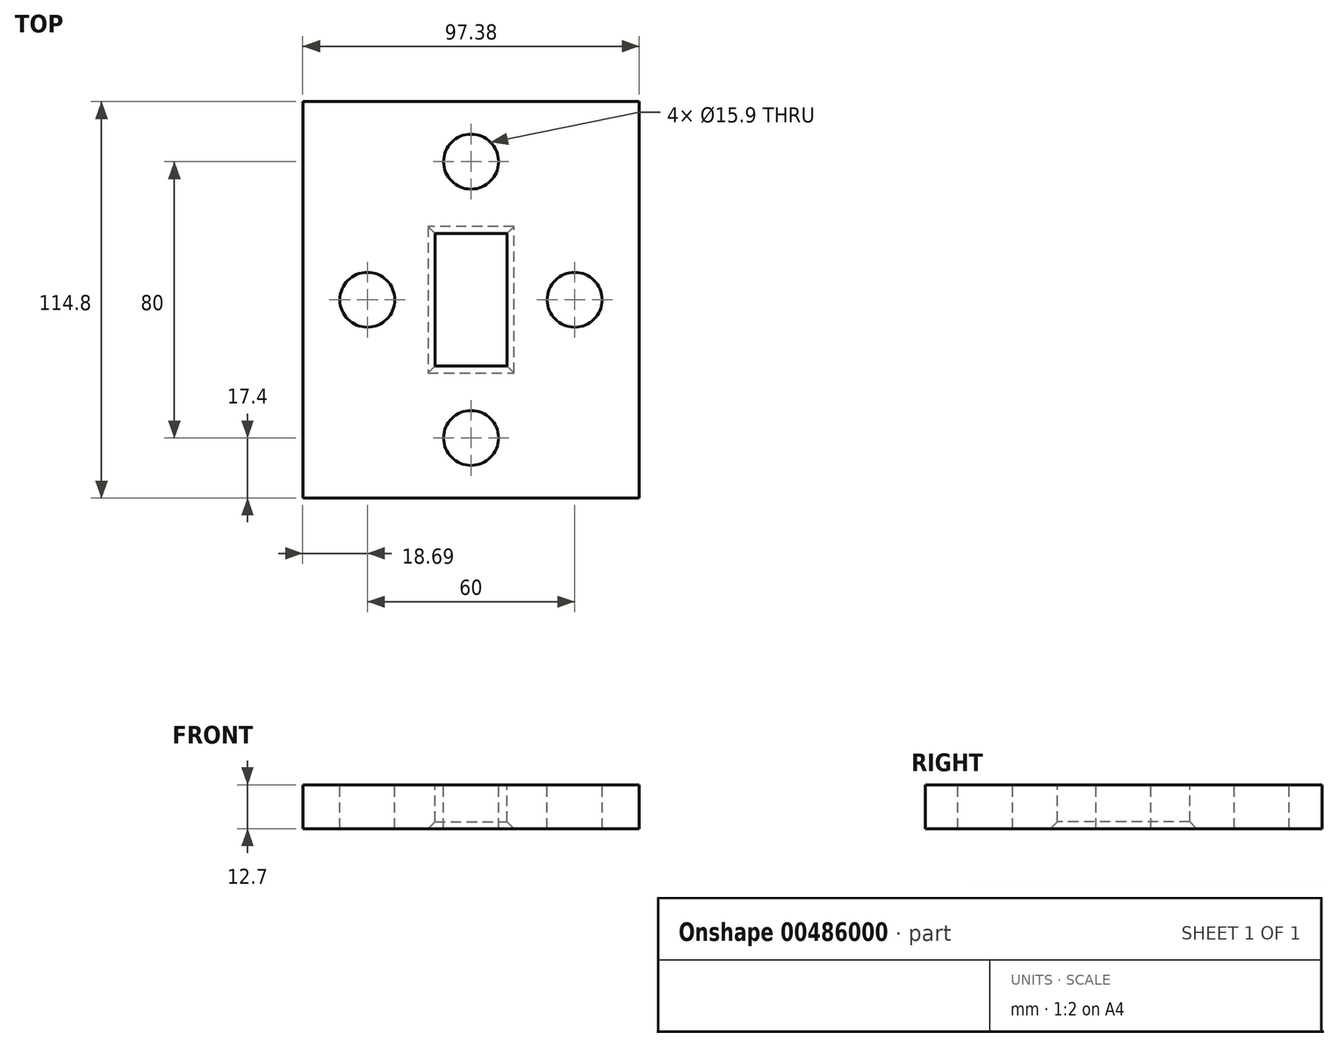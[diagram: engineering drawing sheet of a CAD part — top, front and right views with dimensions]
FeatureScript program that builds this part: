
annotation { "Feature Type Name" : "Feature", "Feature Type Description" : "" }
export const myFeature = defineFeature(function(context is Context, id is Id, definition is map)
    precondition{}
    {
        {
            var Q0;
            Q0=qCreatedBy(makeId("Top.planeOp"),FACE);
            var sketch = newSketch(context, id + "F0", { "sketchPlane" : qUnion([Q0])});
            skLineSegment(sketch, "E0.bottom", {"start": v(48.69, -57.4) * mm, "end": v(-48.69, -57.4) * mm});
            skLineSegment(sketch, "E0.top", {"start": v(48.69, 57.4) * mm, "end": v(-48.69, 57.4) * mm});
            skLineSegment(sketch, "E0.left", {"start": v(48.69, -57.4) * mm, "end": v(48.69, 57.4) * mm});
            skLineSegment(sketch, "E0.right", {"start": v(-48.69, -57.4) * mm, "end": v(-48.69, 57.4) * mm});
            skPoint(sketch, "E0.middle", {"position": v(0, 0) * mm});
            skSolve(sketch);
        }
        {
            var Q0;
            Q0 = qSketchRegion(id + "F0", true);
            extrude(context, id + "F1", {"entities" : qUnion([Q0]), "oppositeDirection" : true, "depth" : 12.7 * mm});
        }
        {
            var Q0;
            Q0=makeQuery(id+"F1.opExtrude","CAP_FACE",FACE,{"disambiguationData":[OSD([sQuery(id+"F0.wireOp",EDGE,"E0.bottom"),sQuery(id+"F0.wireOp",EDGE,"E0.top"),sQuery(id+"F0.wireOp",EDGE,"E0.left"),sQuery(id+"F0.wireOp",EDGE,"E0.right")])],"isStart":true});
            var sketch = newSketch(context, id + "F2", { "sketchPlane" : qUnion([Q0])});
            skLineSegment(sketch, "E1.bottom", {"start": v(10.47, 19.18) * mm, "end": v(-10.46, 19.18) * mm});
            skLineSegment(sketch, "E1.top", {"start": v(10.46, -19.18) * mm, "end": v(-10.47, -19.18) * mm});
            skLineSegment(sketch, "E1.left", {"start": v(10.47, 19.18) * mm, "end": v(10.46, -19.18) * mm});
            skLineSegment(sketch, "E1.right", {"start": v(-10.46, 19.18) * mm, "end": v(-10.47, -19.18) * mm});
            skPoint(sketch, "E1.middle", {"position": v(0, 0) * mm});
            skSolve(sketch);
        }
        {
            var Q0;
            Q0 = qSketchRegion(id + "F2", true);
            extrude(context, id + "F3", {"entities" : qUnion([Q0]), "operationType" : NewBodyOperationType.REMOVE, "endBound" : BoundingType.THROUGH_ALL, "oppositeDirection" : true, "depth" : 25 * mm});
        }
        {
            var Q0;
            Q0=makeQuery(id+"F3.boolean.opBoolean","INTERSECT",EDGE,{"derivedFrom":[makeQuery(id+"F1.opExtrude","CAP_FACE",FACE,{"disambiguationData":[OSD([sQuery(id+"F0.wireOp",EDGE,"E0.bottom"),sQuery(id+"F0.wireOp",EDGE,"E0.top"),sQuery(id+"F0.wireOp",EDGE,"E0.left"),sQuery(id+"F0.wireOp",EDGE,"E0.right")])],"isStart":false}),makeQuery(id+"F3.opExtrude","SWEPT_FACE",FACE,{"disambiguationData":[OSD([sQuery(id+"F2.wireOp",EDGE,"E1.bottom")])]})]});
            var Q1;
            Q1=makeQuery(id+"F3.boolean.opBoolean","INTERSECT",EDGE,{"derivedFrom":[makeQuery(id+"F1.opExtrude","CAP_FACE",FACE,{"disambiguationData":[OSD([sQuery(id+"F0.wireOp",EDGE,"E0.bottom"),sQuery(id+"F0.wireOp",EDGE,"E0.top"),sQuery(id+"F0.wireOp",EDGE,"E0.left"),sQuery(id+"F0.wireOp",EDGE,"E0.right")])],"isStart":false}),makeQuery(id+"F3.opExtrude","SWEPT_FACE",FACE,{"disambiguationData":[OSD([sQuery(id+"F2.wireOp",EDGE,"E1.left")])]})]});
            var Q2;
            Q2=makeQuery(id+"F3.boolean.opBoolean","INTERSECT",EDGE,{"derivedFrom":[makeQuery(id+"F1.opExtrude","CAP_FACE",FACE,{"disambiguationData":[OSD([sQuery(id+"F0.wireOp",EDGE,"E0.bottom"),sQuery(id+"F0.wireOp",EDGE,"E0.top"),sQuery(id+"F0.wireOp",EDGE,"E0.left"),sQuery(id+"F0.wireOp",EDGE,"E0.right")])],"isStart":false}),makeQuery(id+"F3.opExtrude","SWEPT_FACE",FACE,{"disambiguationData":[OSD([sQuery(id+"F2.wireOp",EDGE,"E1.right")])]})]});
            var Q3;
            Q3=makeQuery(id+"F3.boolean.opBoolean","INTERSECT",EDGE,{"derivedFrom":[makeQuery(id+"F1.opExtrude","CAP_FACE",FACE,{"disambiguationData":[OSD([sQuery(id+"F0.wireOp",EDGE,"E0.bottom"),sQuery(id+"F0.wireOp",EDGE,"E0.top"),sQuery(id+"F0.wireOp",EDGE,"E0.left"),sQuery(id+"F0.wireOp",EDGE,"E0.right")])],"isStart":false}),makeQuery(id+"F3.opExtrude","SWEPT_FACE",FACE,{"disambiguationData":[OSD([sQuery(id+"F2.wireOp",EDGE,"E1.top")])]})]});
            chamfer(context, id + "F4", {"entities" : qUnion([Q0, Q1, Q2, Q3]), "width" : 2 * mm, "tangentPropagation" : true});
        }
        {
            var Q0;
            Q0=makeQuery(id+"F1.opExtrude","CAP_FACE",FACE,{"disambiguationData":[OSD([sQuery(id+"F0.wireOp",EDGE,"E0.bottom"),sQuery(id+"F0.wireOp",EDGE,"E0.top"),sQuery(id+"F0.wireOp",EDGE,"E0.left"),sQuery(id+"F0.wireOp",EDGE,"E0.right")])],"isStart":true});
            var sketch = newSketch(context, id + "F5", { "sketchPlane" : qUnion([Q0])});
            skCircle(sketch, "E2", {"center": v(0, 40) * mm, "radius": 7.95 * mm});
            skCircle(sketch, "E3", {"center": v(0, -40) * mm, "radius": 7.95 * mm});
            skCircle(sketch, "E4", {"center": v(30, 0) * mm, "radius": 7.95 * mm});
            skCircle(sketch, "E5", {"center": v(-30, 0) * mm, "radius": 7.95 * mm});
            skPoint(sketch, "E5.centerSnap0", {"position": v(-10.46, 0) * mm});
            skSolve(sketch);
        }
        {
            var Q0;
            Q0=makeQuery(id+"F5.imprint","IMPRINT",FACE,{"disambiguationData":[TD([[makeQuery(id+"F5.imprint","IMPRINT",EDGE,{"derivedFrom":sQuery(id+"F5.wireOp",EDGE,"E2")}),1.0]])]});
            var Q1;
            Q1=makeQuery(id+"F5.imprint","IMPRINT",FACE,{"disambiguationData":[TD([[makeQuery(id+"F5.imprint","IMPRINT",EDGE,{"derivedFrom":sQuery(id+"F5.wireOp",EDGE,"E4")}),1.0]])]});
            var Q2;
            Q2=makeQuery(id+"F5.imprint","IMPRINT",FACE,{"disambiguationData":[TD([[makeQuery(id+"F5.imprint","IMPRINT",EDGE,{"derivedFrom":sQuery(id+"F5.wireOp",EDGE,"E5")}),1.0]])]});
            var Q3;
            Q3=makeQuery(id+"F5.imprint","IMPRINT",FACE,{"disambiguationData":[TD([[makeQuery(id+"F5.imprint","IMPRINT",EDGE,{"derivedFrom":sQuery(id+"F5.wireOp",EDGE,"E3")}),1.0]])]});
            extrude(context, id + "F6", {"entities" : qUnion([Q0, Q1, Q2, Q3]), "operationType" : NewBodyOperationType.REMOVE, "endBound" : BoundingType.THROUGH_ALL, "oppositeDirection" : true, "depth" : 25 * mm});
        }
    });
